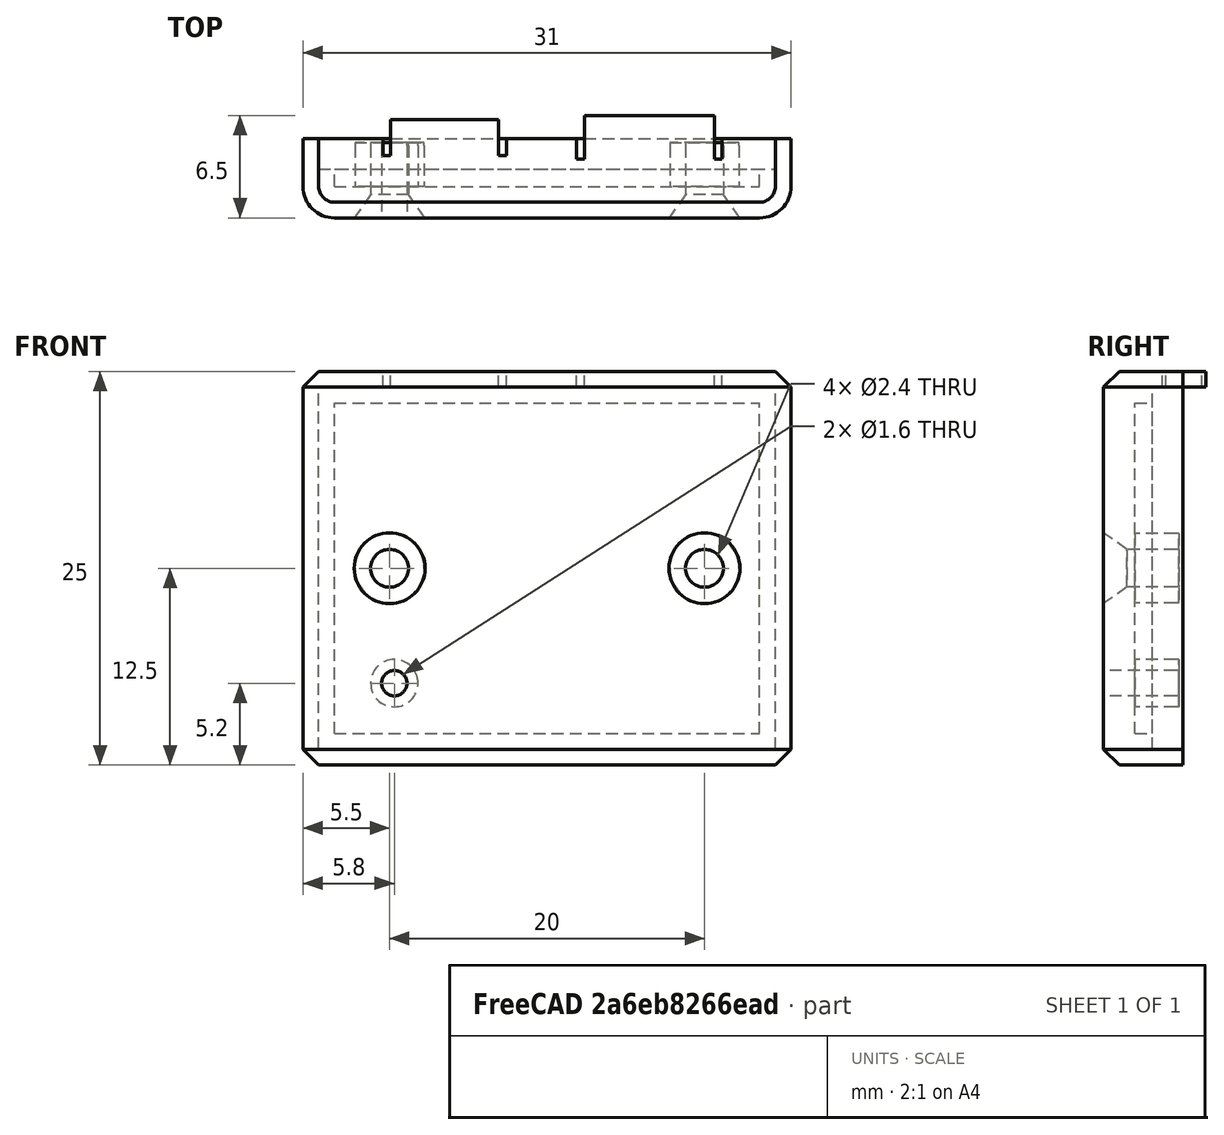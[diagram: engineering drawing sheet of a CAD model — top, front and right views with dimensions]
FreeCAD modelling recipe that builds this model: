
FCSTD DOCUMENT  (FreeCAD 0.18R16110 (Git))
Label: housing_v5_back
License: All rights reserved
LicenseURL: http://en.wikipedia.org/wiki/All_rights_reserved
objects: Part::Box×10, Part::MultiFuse×10, Part::Cut×8, Part::Cylinder×6, Part::Feature×5, Part::Extrusion×5, Part::Cone×2, Part::Fillet×1, Part::Chamfer×1
note: 48 computed .brp shape members not serialized (recipe doc carries the construction recipe); baked Part::Feature solids carry a one-line shape summary decoded from their .brp

FEATURE [Part::Box] Box  label="base"
  AttacherType = Attacher::AttachEngine3D
  Height = 25
  Length = 31
  Width = 4.6
FEATURE [Part::Box] Box001  label="innerCut"
  AttacherType = Attacher::AttachEngine3D
  Height = 21
  Length = 27
  Placement = pos=(2,2,2) rot=(0,0,1;0rad)
  Width = 2.6
FEATURE [Part::Cut] Cut  label="case"
  Base = -> Box
  Tool = -> Box001
FEATURE [Part::Cylinder] Cylinder  label="pcbHolder"
  Angle = 360
  AttacherType = Attacher::AttachEngine3D
  Height = 2.6
  Placement = pos=(25.5,4.6,12.5) rot=(1,0,0;1.5708rad)
  Radius = 2.2
FEATURE [Part::Cylinder] Cylinder001  label="pcbHolderHole"
  Angle = 360
  AttacherType = Attacher::AttachEngine3D
  Height = 10.6
  Placement = pos=(25.5,4.6,12.5) rot=(1,0,0;1.5708rad)
  Radius = 1.2
FEATURE [Part::Cylinder] Cylinder002  label="pcbHolderHole001"
  Angle = 360
  AttacherType = Attacher::AttachEngine3D
  Height = 10.6
  Placement = pos=(5.5,4.6,12.5) rot=(1,0,0;1.5708rad)
  Radius = 1.2
FEATURE [Part::Cylinder] Cylinder003  label="pcbHolder001"
  Angle = 360
  AttacherType = Attacher::AttachEngine3D
  Height = 2.6
  Placement = pos=(5.5,4.6,12.5) rot=(1,0,0;1.5708rad)
  Radius = 2.2
FEATURE [Part::MultiFuse] Fusion  label="caseWithPcbHolder"
  Shapes = -> [Cylinder,Cylinder003,Cut]
FEATURE [Part::MultiFuse] Fusion001  label="pcbHoles"
  Shapes = -> [Cylinder001,Cylinder002]
FEATURE [Part::Cut] Cut001  label="caseWithHoles"
  Base = -> Fusion
  Tool = -> Fusion001
FEATURE [Part::Cylinder] Cylinder004  label="bootloaderHole"
  Angle = 360
  AttacherType = Attacher::AttachEngine3D
  Height = 20.6
  Placement = pos=(5.8,12,5.2) rot=(1,0,0;1.5708rad)
  Radius = 0.8
FEATURE [Part::Cylinder] Cylinder005  label="bootloderCanal"
  Angle = 360
  AttacherType = Attacher::AttachEngine3D
  Height = 2.6
  Placement = pos=(5.8,4.6,5.2) rot=(1,0,0;1.5708rad)
  Radius = 1.5
FEATURE [Part::MultiFuse] Fusion002  label="caseFusion"
  Shapes = -> [Cylinder005,Cut001]
FEATURE [Part::Cut] Cut002  label="caseWithBootloaderHole"
  Base = -> Fusion002
  Tool = -> Cylinder004
FEATURE [Part::Box] Box002  label="Cube"
  AttacherType = Attacher::AttachEngine3D
  Height = 23
  Length = 29
  Placement = pos=(1,3.1,1) rot=(0,0,1;0rad)
  Width = 1.5
FEATURE [Part::Box] Box003  label="Cube001"
  AttacherType = Attacher::AttachEngine3D
  Height = 21
  Length = 27
  Placement = pos=(2,3.1,2) rot=(0,0,1;0rad)
  Width = 1.5
FEATURE [Part::Cut] Cut004
  Base = -> Box002
  Tool = -> Box003
FEATURE [Part::Box] Box004  label="Cube002"
  AttacherType = Attacher::AttachEngine3D
  Height = 25
  Length = 31
  Placement = pos=(0,4.6,0) rot=(0,0,1;0rad)
  Width = 0.45
FEATURE [Part::Box] Box005  label="Cube003"
  AttacherType = Attacher::AttachEngine3D
  Height = 23
  Length = 29
  Placement = pos=(1,4.6,1) rot=(0,0,1;0rad)
  Width = 0.45
FEATURE [Part::Cut] Cut006
  Base = -> Box004
  Tool = -> Box005
FEATURE [Part::Cone] Cone  label="counterSunkLeft"
  Angle = 360
  AttacherType = Attacher::AttachEngine3D
  Height = 1.5
  Placement = pos=(5.5,0,12.5) rot=(-1,0,0;1.5708rad)
  Radius1 = 2.25
  Radius2 = 1.2
FEATURE [Part::Cone] Cone001  label="counterSunkRight"
  Angle = 360
  AttacherType = Attacher::AttachEngine3D
  Height = 1.5
  Placement = pos=(25.5,0,12.5) rot=(-1,0,0;1.5708rad)
  Radius1 = 2.25
  Radius2 = 1.2
FEATURE [Part::MultiFuse] Fusion005  label="counterSunk"
  Shapes = -> [Cone001,Cone]
FEATURE [Part::Cut] Cut009
  Base = -> Cut002
  Tool = -> Cut004
FEATURE [Part::MultiFuse] Fusion004  label="caseWithEdge"
  Shapes = -> [Cut006,Cut009]
FEATURE [Part::Box] Box006  label="TypeC_cutout"
  AttacherType = Attacher::AttachEngine3D
  Height = 10
  Length = 9.25
  Placement = pos=(17.37,3.75,19) rot=(0,0,1;0rad)
  Width = 2.55
FEATURE [Part::Box] Box007  label="Micro_cutout"
  AttacherType = Attacher::AttachEngine3D
  Height = 10
  Length = 7.85
  Placement = pos=(5.07,3.95,20) rot=(0,0,1;0rad)
  Width = 2.1
FEATURE [Part::MultiFuse] Fusion006  label="connector_cutouts"
  Shapes = -> [Box006,Box007]
FEATURE [Part::Cut] Cut010
  Base = -> Fusion004
  Tool = -> Fusion006
FEATURE [Part::Cut] Cut011
  Base = -> Cut010
  Tool = -> Fusion005
FEATURE [Part::Box] Box008  label="TypeC_cutoff"
  AttacherType = Attacher::AttachEngine3D
  Height = 1
  Length = 8.25
  Placement = pos=(17.87,3.75,24) rot=(0,0,1;0rad)
  Width = 2.55
FEATURE [Part::Box] Box009  label="Micro_cutoff"
  AttacherType = Attacher::AttachEngine3D
  Height = 1
  Length = 6.85
  Placement = pos=(5.57,3.95,24) rot=(0,0,1;0rad)
  Width = 2.1
FEATURE [Part::MultiFuse] Fusion007
  Shapes = -> [Cut011,Box008,Box009]
FEATURE [Part::Fillet] Fillet
  Base = -> Fusion007
  Edges = 2 edges r=2: [Edge5,Edge24]
FEATURE [Part::Chamfer] Chamfer
  Base = -> Fillet
  Edges = 14 edges r=1: [Edge1,Edge4,Edge5,Edge7,Edge9,Edge11,Edge22,Edge24,Edge26,Edge28,Edge29,Edge30,Edge50,Edge82]
FEATURE [Part::Feature] Face
  shape: bbox 4.4 x 2e-07 x 4.4 mm, 1 faces, 0 solids (baked)
FEATURE [Part::Extrusion] Extrusion
  Base = -> Face
  Dir = (0,0.2,0)
  DirMode = 0
  FaceMakerClass = Part::FaceMakerBullseye
  LengthFwd = 0
  LengthRev = 0
  Solid = true
  Symmetric = false
FEATURE [Part::Feature] Face001
  shape: bbox 4.4 x 2e-07 x 4.4 mm, 1 faces, 0 solids (baked)
FEATURE [Part::Extrusion] Extrusion001
  Base = -> Face001
  Dir = (0,0.2,0)
  DirMode = 0
  FaceMakerClass = Part::FaceMakerBullseye
  LengthFwd = 0
  LengthRev = 0
  Solid = true
  Symmetric = false
FEATURE [Part::Feature] Face003
  shape: bbox 3 x 2e-07 x 3 mm, 1 faces, 0 solids (baked)
FEATURE [Part::Extrusion] Extrusion002
  Base = -> Face003
  Dir = (0,0.2,0)
  DirMode = 0
  FaceMakerClass = Part::FaceMakerBullseye
  LengthFwd = 0
  LengthRev = 0
  Solid = true
  Symmetric = false
FEATURE [Part::MultiFuse] Fusion008
  Shapes = -> [Extrusion,Extrusion001,Extrusion002]
FEATURE [Part::MultiFuse] Fusion009
  Shapes = -> [Fusion008,Chamfer]
FEATURE [Part::Feature] Face004
  Placement = pos=(17.87,3.75,24) rot=(0,0,1;0rad)
  shape: bbox 8.25 x 2e-07 x 1 mm, 1 faces, 0 solids (baked)
FEATURE [Part::Extrusion] Extrusion003
  Base = -> Face004
  Dir = (0,0.2,0)
  DirMode = 0
  FaceMakerClass = Part::FaceMakerBullseye
  LengthFwd = 0
  LengthRev = 0
  Solid = true
  Symmetric = false
FEATURE [Part::Feature] Face005
  Placement = pos=(5.57,3.95,24) rot=(0,0,1;0rad)
  shape: bbox 6.85 x 2e-07 x 1 mm, 1 faces, 0 solids (baked)
FEATURE [Part::Extrusion] Extrusion004
  Base = -> Face005
  Dir = (0,0.2,0)
  DirMode = 0
  FaceMakerClass = Part::FaceMakerBullseye
  LengthFwd = 0
  LengthRev = 0
  Solid = true
  Symmetric = false
FEATURE [Part::MultiFuse] Fusion010
  Shapes = -> [Fusion009,Extrusion003,Extrusion004]
